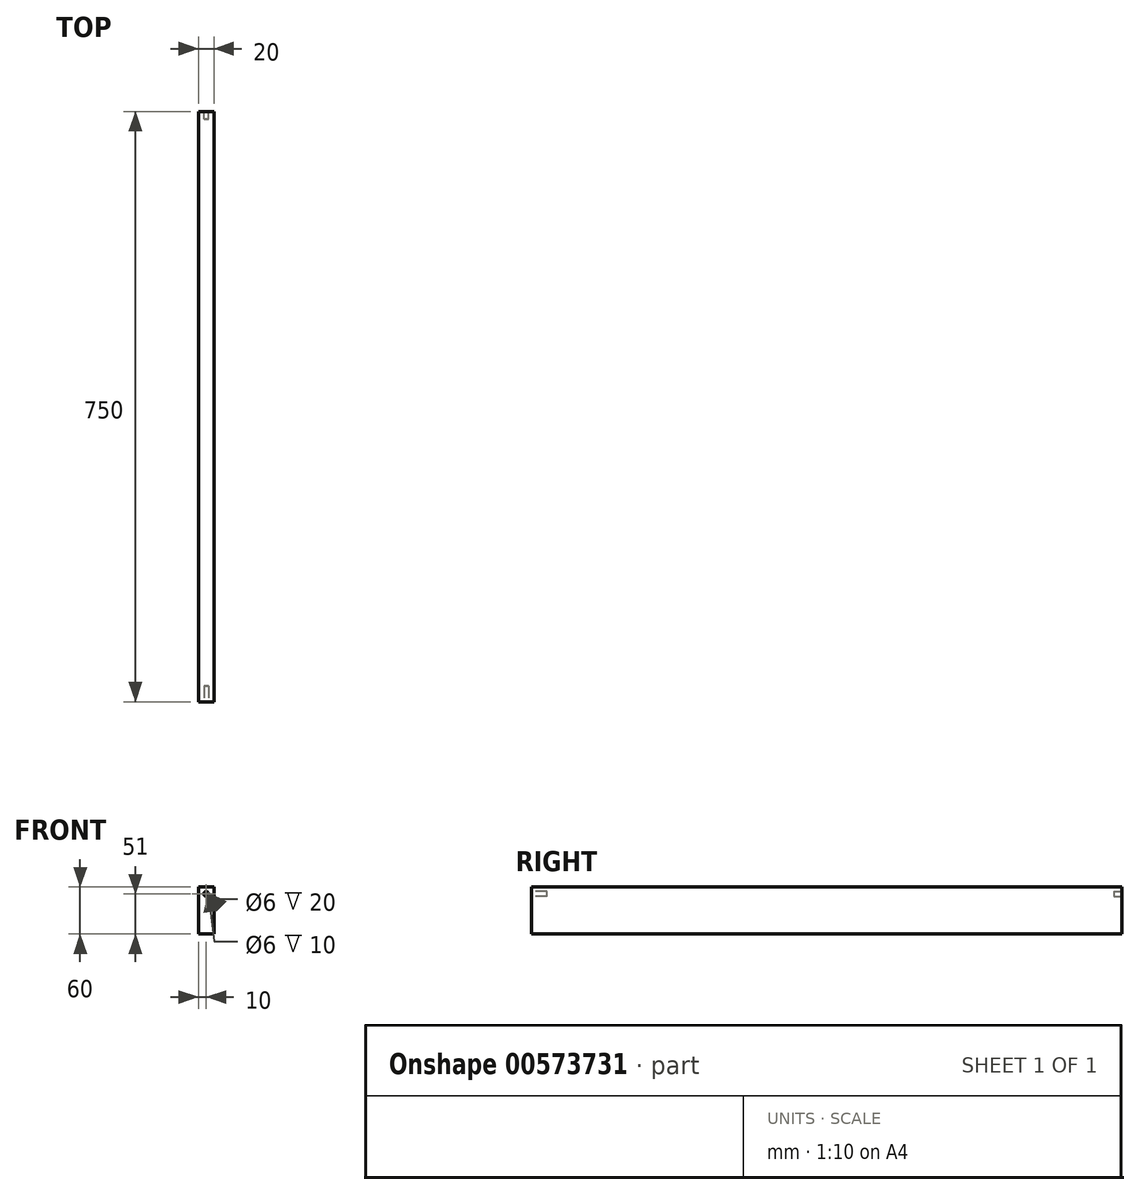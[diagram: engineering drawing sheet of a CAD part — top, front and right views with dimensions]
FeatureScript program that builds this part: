
annotation { "Feature Type Name" : "Feature", "Feature Type Description" : "" }
export const myFeature = defineFeature(function(context is Context, id is Id, definition is map)
    precondition{}
    {
        {
            var Q0;
            Q0=qCreatedBy(makeId("Front.planeOp"),FACE);
            var sketch = newSketch(context, id + "F0", { "sketchPlane" : qUnion([Q0])});
            skLineSegment(sketch, "E0.bottom", {"start": v(0, 0) * mm, "end": v(20, 0) * mm});
            skLineSegment(sketch, "E0.top", {"start": v(0, 60) * mm, "end": v(20, 60) * mm});
            skLineSegment(sketch, "E0.left", {"start": v(0, 0) * mm, "end": v(0, 60) * mm});
            skLineSegment(sketch, "E0.right", {"start": v(20, 0) * mm, "end": v(20, 60) * mm});
            skSolve(sketch);
        }
        {
            var Q0;
            Q0 = qSketchRegion(id + "F0", true);
            extrude(context, id + "F1", {"entities" : qUnion([Q0]), "oppositeDirection" : true, "depth" : 750 * mm, "offsetDistance" : 25 * mm});
        }
        {
            var Q0;
            Q0=makeQuery(id+"F1.opExtrude","CAP_FACE",FACE,{"disambiguationData":[OSD([sQuery(id+"F0.wireOp",EDGE,"E0.bottom"),sQuery(id+"F0.wireOp",EDGE,"E0.top"),sQuery(id+"F0.wireOp",EDGE,"E0.left"),sQuery(id+"F0.wireOp",EDGE,"E0.right")])],"isStart":true});
            var sketch = newSketch(context, id + "F2", { "sketchPlane" : qUnion([Q0])});
            skCircle(sketch, "E1", {"center": v(10, 51) * mm, "radius": 3 * mm});
            skSolve(sketch);
        }
        {
            var Q0;
            Q0 = qSketchRegion(id + "F2", true);
            extrude(context, id + "F3", {"entities" : qUnion([Q0]), "operationType" : NewBodyOperationType.REMOVE, "oppositeDirection" : true, "depth" : 20 * mm, "offsetDistance" : 25 * mm});
        }
        {
            var Q0;
            Q0=makeQuery(id+"F1.opExtrude","CAP_FACE",FACE,{"disambiguationData":[OSD([sQuery(id+"F0.wireOp",EDGE,"E0.bottom"),sQuery(id+"F0.wireOp",EDGE,"E0.top"),sQuery(id+"F0.wireOp",EDGE,"E0.left"),sQuery(id+"F0.wireOp",EDGE,"E0.right")])],"isStart":false});
            var sketch = newSketch(context, id + "F4", { "sketchPlane" : qUnion([Q0])});
            skCircle(sketch, "E2", {"center": v(-10, 51) * mm, "radius": 3 * mm});
            skSolve(sketch);
        }
        {
            var Q0;
            Q0 = qSketchRegion(id + "F4", true);
            extrude(context, id + "F5", {"entities" : qUnion([Q0]), "operationType" : NewBodyOperationType.REMOVE, "oppositeDirection" : true, "depth" : 10 * mm, "offsetDistance" : 25 * mm});
        }
    });
